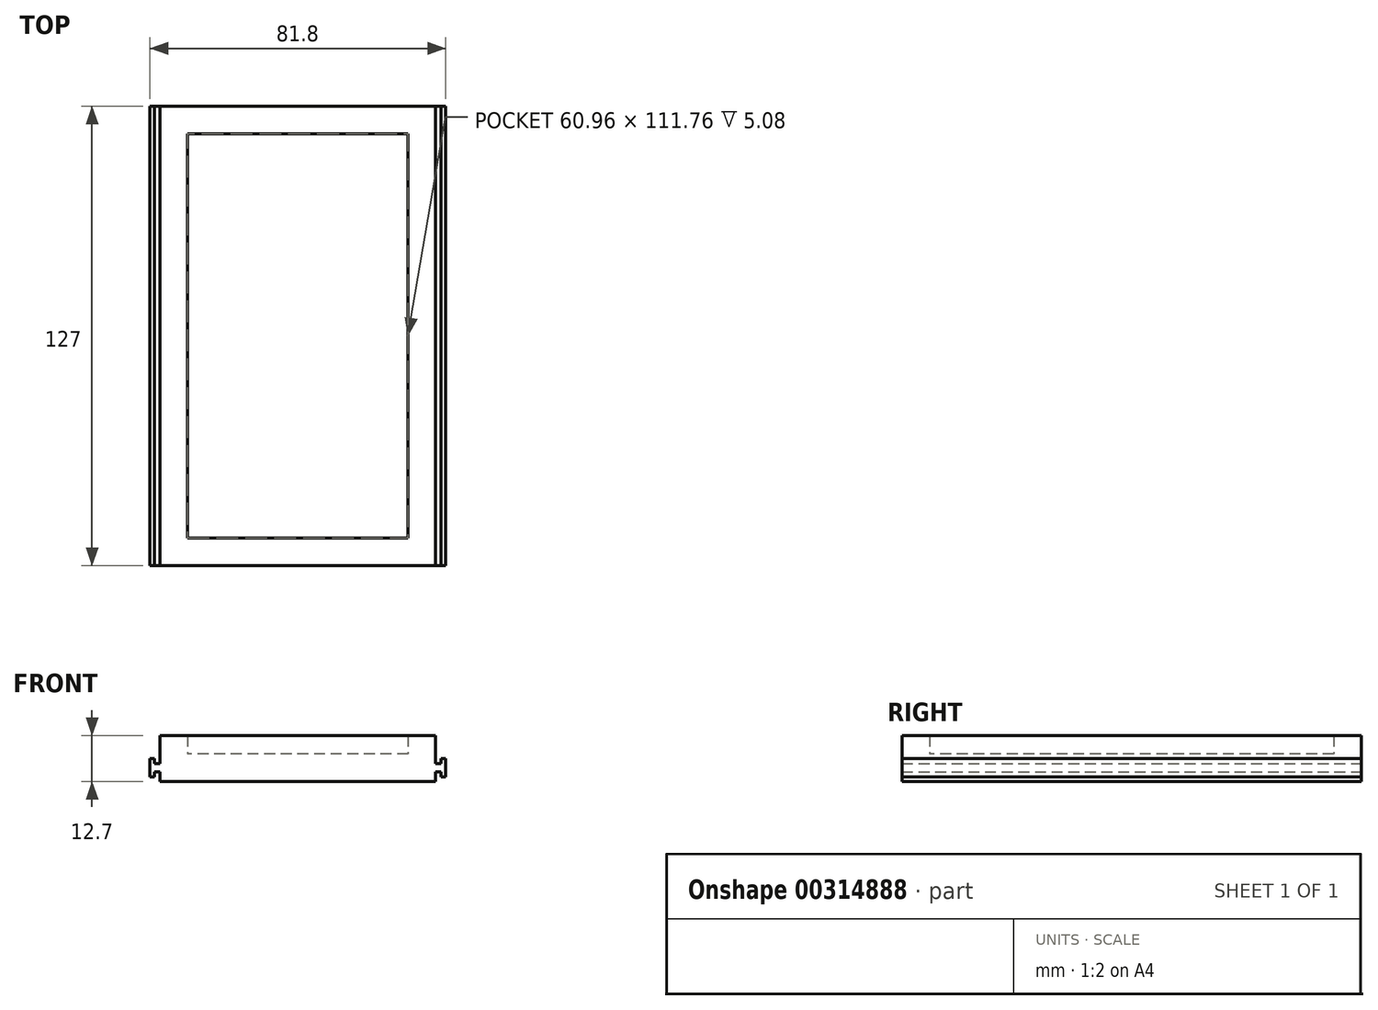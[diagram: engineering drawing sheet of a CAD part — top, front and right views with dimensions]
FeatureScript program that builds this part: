
annotation { "Feature Type Name" : "Feature", "Feature Type Description" : "" }
export const myFeature = defineFeature(function(context is Context, id is Id, definition is map)
    precondition{}
    {
        {
            var Q0;
            Q0=qCreatedBy(makeId("Top.planeOp"),FACE);
            var sketch = newSketch(context, id + "F0", { "sketchPlane" : qUnion([Q0])});
            skLineSegment(sketch, "E0.bottom", {"start": v(38.1, 63.5) * mm, "end": v(-38.1, 63.5) * mm});
            skLineSegment(sketch, "E0.top", {"start": v(38.1, -63.5) * mm, "end": v(-38.1, -63.5) * mm});
            skLineSegment(sketch, "E0.left", {"start": v(38.1, 63.5) * mm, "end": v(38.1, -63.5) * mm});
            skLineSegment(sketch, "E0.right", {"start": v(-38.1, 63.5) * mm, "end": v(-38.1, -63.5) * mm});
            skPoint(sketch, "E0.middle", {"position": v(0, 0) * mm});
            skSolve(sketch);
        }
        {
            var Q0;
            Q0=qSketchRegion(id+"F0",true);
            extrude(context, id + "F1", {"entities" : qUnion([Q0]), "depth" : 12.7 * mm});
        }
        {
            var Q0;
            Q0=makeQuery(id+"F1.opExtrude","CAP_FACE",FACE,{"disambiguationData":[OSD([sQuery(id+"F0.wireOp",EDGE,"E0.bottom"),sQuery(id+"F0.wireOp",EDGE,"E0.top"),sQuery(id+"F0.wireOp",EDGE,"E0.left"),sQuery(id+"F0.wireOp",EDGE,"E0.right")])],"isStart":false});
            shell(context, id + "F2", {"entities" : qUnion([Q0]), "thickness" : 7.62 * mm});
        }
        {
            var Q0;
            Q0=qCreatedBy(makeId("Front.planeOp"),FACE);
            var sketch = newSketch(context, id + "F3", { "sketchPlane" : qUnion([Q0])});
            skLineSegment(sketch, "E1.MirrorCS", {"start": v(-39.63, 4.95) * mm, "end": v(-39.63, 2.67) * mm});
            skPoint(sketch, "E2.MirrorP", {"position": v(-39.63, 3.81) * mm});
            skLineSegment(sketch, "E3.MirrorCS", {"start": v(-39.63, 6.35) * mm, "end": v(-39.63, 1.27) * mm});
            skLineSegment(sketch, "E4.MirrorCS", {"start": v(-40.9, 6.35) * mm, "end": v(-40.9, 1.27) * mm});
            skLineSegment(sketch, "E5.MirrorCS", {"start": v(-38.1, 4.95) * mm, "end": v(-39.63, 4.95) * mm});
            skLineSegment(sketch, "E6.MirrorCS", {"start": v(-39.63, 1.27) * mm, "end": v(-40.9, 1.27) * mm});
            skLineSegment(sketch, "E7.MirrorCS", {"start": v(-38.1, 2.67) * mm, "end": v(-39.63, 2.67) * mm});
            skLineSegment(sketch, "E8.MirrorCS", {"start": v(-38.1, 4.95) * mm, "end": v(-38.1, 2.67) * mm});
            skLineSegment(sketch, "E9.MirrorCS", {"start": v(-39.63, 6.35) * mm, "end": v(-40.9, 6.35) * mm});
            skLineSegment(sketch, "E10", {"start": v(-38.1, 0) * mm, "end": v(-38.1, 3.81) * mm});
            skPoint(sketch, "E11", {"position": v(-38.1, 3.81) * mm});
            skLineSegment(sketch, "E12.MirrorCS", {"start": v(39.63, 4.95) * mm, "end": v(39.63, 2.67) * mm});
            skLineSegment(sketch, "E13.MirrorCS", {"start": v(38.1, 2.67) * mm, "end": v(39.63, 2.67) * mm});
            skLineSegment(sketch, "E14.MirrorCS", {"start": v(39.63, 1.27) * mm, "end": v(40.9, 1.27) * mm});
            skLineSegment(sketch, "E15.MirrorCS", {"start": v(38.1, 4.95) * mm, "end": v(39.63, 4.95) * mm});
            skLineSegment(sketch, "E16.MirrorCS", {"start": v(40.9, 6.35) * mm, "end": v(40.9, 1.27) * mm});
            skLineSegment(sketch, "E17.MirrorCS", {"start": v(39.63, 6.35) * mm, "end": v(39.63, 1.27) * mm});
            skLineSegment(sketch, "E18.MirrorCS", {"start": v(38.1, 0) * mm, "end": v(38.1, 3.81) * mm});
            skLineSegment(sketch, "E19.MirrorCS", {"start": v(38.1, 4.95) * mm, "end": v(38.1, 2.67) * mm});
            skLineSegment(sketch, "E20.MirrorCS", {"start": v(39.63, 6.35) * mm, "end": v(40.9, 6.35) * mm});
            skPoint(sketch, "E21.MirrorP", {"position": v(39.63, 3.81) * mm});
            skPoint(sketch, "E22.MirrorP", {"position": v(38.1, 3.81) * mm});
            skSolve(sketch);
        }
        {
            var Q0;
            Q0=qSketchRegion(id+"F3",true);
            extrude(context, id + "F4", {"entities" : qUnion([Q0]), "operationType" : NewBodyOperationType.ADD, "endBound" : BoundingType.SYMMETRIC, "depth" : 127 * mm});
        }
    });
